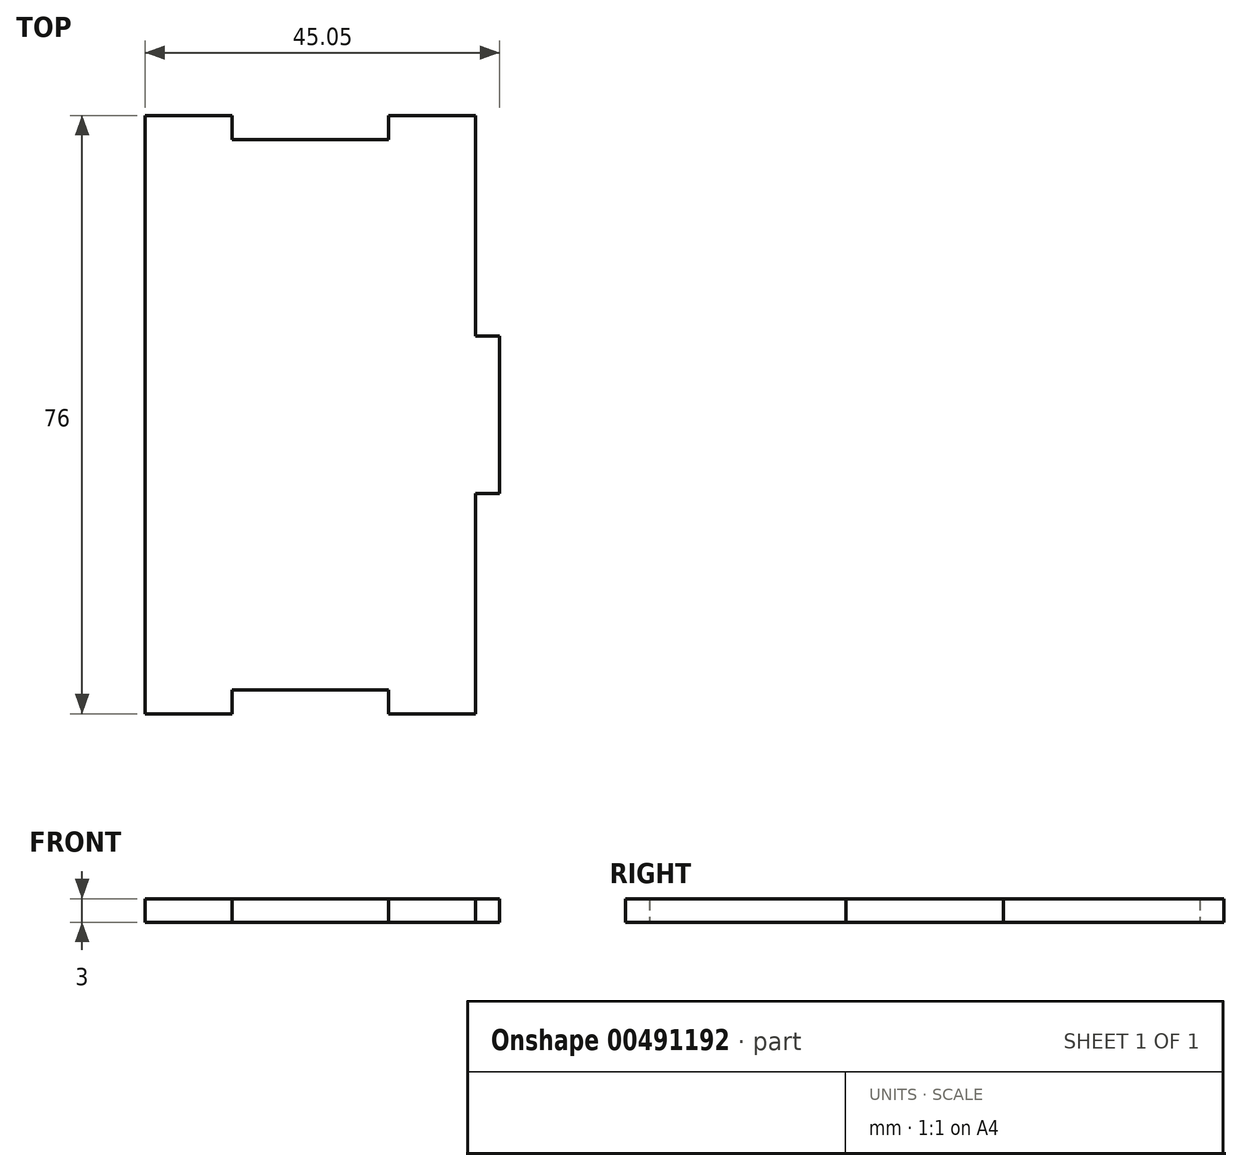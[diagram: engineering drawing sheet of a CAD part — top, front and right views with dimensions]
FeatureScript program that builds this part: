
annotation { "Feature Type Name" : "Feature", "Feature Type Description" : "" }
export const myFeature = defineFeature(function(context is Context, id is Id, definition is map)
    precondition{}
    {
        {
            var Q0;
            Q0=qCreatedBy(makeId("Top.planeOp"),FACE);
            var sketch = newSketch(context, id + "F0", { "sketchPlane" : qUnion([Q0])});
            skLineSegment(sketch, "E0.bottom", {"start": v(21, -38) * mm, "end": v(-21, -38) * mm});
            skLineSegment(sketch, "E0.top", {"start": v(21, 38) * mm, "end": v(-21, 38) * mm});
            skLineSegment(sketch, "E0.left", {"start": v(21, -38) * mm, "end": v(21, 38) * mm});
            skLineSegment(sketch, "E0.right", {"start": v(-21, -38) * mm, "end": v(-21, 38) * mm});
            skPoint(sketch, "E0.middle", {"position": v(0, 0) * mm});
            skLineSegment(sketch, "E1.bottom", {"start": v(24.05, -10) * mm, "end": v(21, -10) * mm});
            skLineSegment(sketch, "E1.top", {"start": v(24.05, 10) * mm, "end": v(21, 10) * mm});
            skLineSegment(sketch, "E1.left", {"start": v(24.05, -10) * mm, "end": v(24.05, 10) * mm});
            skLineSegment(sketch, "E1.right", {"start": v(21, -10) * mm, "end": v(21, 10) * mm});
            skPoint(sketch, "E1.middle", {"position": v(22.52, 0) * mm});
            skLineSegment(sketch, "E2.bottom", {"start": v(9.95, 34.95) * mm, "end": v(-9.95, 34.95) * mm});
            skLineSegment(sketch, "E2.top", {"start": v(9.95, 38) * mm, "end": v(-9.95, 38) * mm});
            skLineSegment(sketch, "E2.left", {"start": v(9.95, 34.95) * mm, "end": v(9.95, 38) * mm});
            skLineSegment(sketch, "E2.right", {"start": v(-9.95, 34.95) * mm, "end": v(-9.95, 38) * mm});
            skPoint(sketch, "E2.middle", {"position": v(0, 36.48) * mm});
            skLineSegment(sketch, "E3.bottom", {"start": v(9.95, -38) * mm, "end": v(-9.95, -38) * mm});
            skLineSegment(sketch, "E3.top", {"start": v(9.95, -34.95) * mm, "end": v(-9.95, -34.95) * mm});
            skLineSegment(sketch, "E3.left", {"start": v(9.95, -38) * mm, "end": v(9.95, -34.95) * mm});
            skLineSegment(sketch, "E3.right", {"start": v(-9.95, -38) * mm, "end": v(-9.95, -34.95) * mm});
            skPoint(sketch, "E3.middle", {"position": v(0, -36.47) * mm});
            skSolve(sketch);
        }
        {
            var Q0;
            Q0=makeQuery(id+"F0.imprint","IMPRINT",FACE,{"disambiguationData":[TD([[makeQuery(id+"F0.imprint","IMPRINT",EDGE,{"derivedFrom":sQuery(id+"F0.wireOp",EDGE,"E1.bottom")}),-1.0]])]});
            var Q1;
            {var subQ1=sQuery(id+"F0.wireOp",EDGE,"E0.right");Q1=makeQuery(id+"F0.imprint","IMPRINT",FACE,{"disambiguationData":[TD([[makeQuery(id+"F0.imprint","IMPRINT",EDGE,{"derivedFrom":subQ1}),-1.0]])]});}
            extrude(context, id + "F1", {"entities" : qUnion([Q0, Q1]), "depth" : 3 * mm});
        }
    });
